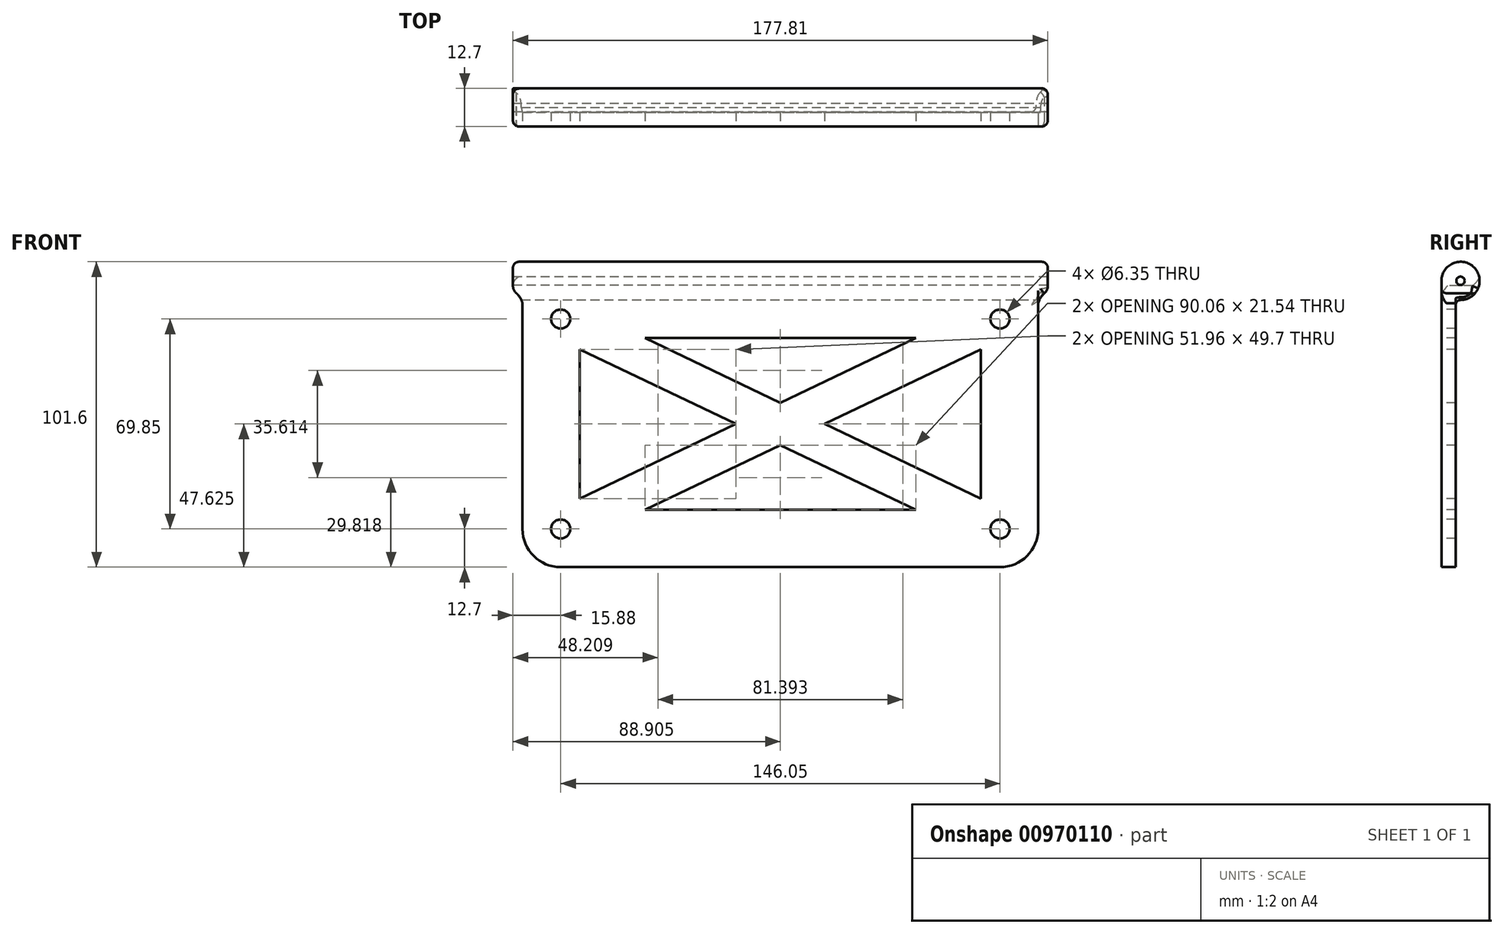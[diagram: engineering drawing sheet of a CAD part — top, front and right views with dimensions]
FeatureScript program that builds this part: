
annotation { "Feature Type Name" : "Feature", "Feature Type Description" : "" }
export const myFeature = defineFeature(function(context is Context, id is Id, definition is map)
    precondition{}
    {
        {
            var Q0;
            Q0=qCreatedBy(makeId("Front.planeOp"),FACE);
            var sketch = newSketch(context, id + "F0", { "sketchPlane" : qUnion([Q0])});
            skLineSegment(sketch, "E0", {"start": v(171.45, 127) * mm, "end": v(12.7, 127) * mm});
            skPoint(sketch, "E1.visualSharp", {"position": v(0, 127) * mm});
            skPoint(sketch, "E2.visualSharp", {"position": v(184.15, 127) * mm});
            skPoint(sketch, "E3.visualSharp", {"position": v(0, 0) * mm});
            skCircle(sketch, "E4", {"center": v(19.05, 107.95) * mm, "radius": 3.17 * mm});
            skCircle(sketch, "E5", {"center": v(165.1, 107.95) * mm, "radius": 3.18 * mm});
            skLineSegment(sketch, "E6", {"start": v(12.7, 127) * mm, "end": v(0, 127) * mm});
            skLineSegment(sketch, "E7", {"start": v(171.45, 127) * mm, "end": v(184.15, 127) * mm});
            skCircle(sketch, "E8", {"center": v(19.05, 38.1) * mm, "radius": 3.18 * mm});
            skCircle(sketch, "E9", {"center": v(165.1, 38.1) * mm, "radius": 3.18 * mm});
            skLineSegment(sketch, "E10", {"start": v(0, 127) * mm, "end": v(0, 25.4) * mm});
            skLineSegment(sketch, "E11", {"start": v(184.15, 127) * mm, "end": v(184.15, 25.4) * mm});
            skLineSegment(sketch, "E12", {"start": v(0, 25.4) * mm, "end": v(184.15, 25.4) * mm});
            skSolve(sketch);
        }
        {
            var Q0;
            Q0=makeQuery(id+"F0.imprint","IMPRINT",FACE,{"disambiguationData":[TD([[makeQuery(id+"F0.imprint","IMPRINT",EDGE,{"derivedFrom":sQuery(id+"F0.wireOp",EDGE,"Pz5NrIL3-ze5f-zlSV-9IkB-DhctpmxIF3Tt")}),1.0]])]});
            var Q1;
            Q1=makeQuery(id+"F0.imprint","IMPRINT",FACE,{"disambiguationData":[TD([[makeQuery(id+"F0.imprint","IMPRINT",EDGE,{"derivedFrom":sQuery(id+"F0.wireOp",EDGE,"E0")}),1.0]])]});
            extrude(context, id + "F1", {"entities" : qUnion([Q0, Q1]), "oppositeDirection" : true, "depth" : 12.7 * mm, "offsetDistance" : 25.4 * mm});
        }
        {
            var Q0;
            Q0=makeQuery(id+"F1.opExtrude","SWEPT_FACE",FACE,{"disambiguationData":[OSD([sQuery(id+"F0.wireOp",EDGE,"E11")])]});
            var sketch = newSketch(context, id + "F2", { "sketchPlane" : qUnion([Q0])});
            skLineSegment(sketch, "E13", {"start": v(6.35, 127) * mm, "end": v(6.35, 120.65) * mm});
            skArc(sketch, "E14", {"start": v(6.36, 114.3) * mm, "mid": v(7.15, 126.95) * mm, "end": v(4.76, 114.5) * mm});
            skLineSegment(sketch, "E15", {"start": v(0, 25.4) * mm, "end": v(4.76, 25.4) * mm});
            skLineSegment(sketch, "E16", {"start": v(4.76, 25.4) * mm, "end": v(4.76, 112.65) * mm});
            skArc(sketch, "E17", {"start": v(6.44, 114.3) * mm, "mid": v(5.26, 113.83) * mm, "end": v(4.76, 112.65) * mm});
            skCircle(sketch, "E18", {"center": v(6.35, 120.65) * mm, "radius": 1.4 * mm});
            skSolve(sketch);
        }
        {
            var Q0;
            Q0=makeQuery(id+"F1.opExtrude","CAP_FACE",FACE,{"disambiguationData":[OSD([sQuery(id+"F0.wireOp",EDGE,"E0"),sQuery(id+"F0.wireOp",EDGE,"E4"),sQuery(id+"F0.wireOp",EDGE,"E5"),sQuery(id+"F0.wireOp",EDGE,"E6"),sQuery(id+"F0.wireOp",EDGE,"E7"),sQuery(id+"F0.wireOp",EDGE,"E8"),sQuery(id+"F0.wireOp",EDGE,"E9"),sQuery(id+"F0.wireOp",EDGE,"E10"),sQuery(id+"F0.wireOp",EDGE,"E11"),sQuery(id+"F0.wireOp",EDGE,"E12")])],"isStart":true});
            var sketch = newSketch(context, id + "F3", { "sketchPlane" : qUnion([Q0])});
            skLineSegment(sketch, "E19", {"start": v(184.15, 127) * mm, "end": v(180.97, 127) * mm});
            skLineSegment(sketch, "E20", {"start": v(0, 127) * mm, "end": v(3.17, 127) * mm});
            skLineSegment(sketch, "E21", {"start": v(3.17, 127) * mm, "end": v(3.17, 118.95) * mm});
            skLineSegment(sketch, "E22", {"start": v(6.35, 25.4) * mm, "end": v(6.35, 113.16) * mm});
            skArc(sketch, "E23", {"start": v(3.17, 119.08) * mm, "mid": v(4.08, 116.8) * mm, "end": v(6.35, 115.84) * mm});
            skArc(sketch, "E24", {"start": v(6.35, 113.16) * mm, "mid": v(5.58, 115.04) * mm, "end": v(4.26, 116.57) * mm});
            skLineSegment(sketch, "E25", {"start": v(180.97, 127) * mm, "end": v(180.97, 118.95) * mm});
            skLineSegment(sketch, "E26", {"start": v(165.1, 38.1) * mm, "end": v(177.8, 38.1) * mm});
            skLineSegment(sketch, "E27", {"start": v(177.8, 25.4) * mm, "end": v(177.8, 127) * mm});
            skLineSegment(sketch, "E28", {"start": v(180.97, 118.95) * mm, "end": v(177.8, 118.95) * mm});
            skCircle(sketch, "E29", {"center": v(177.8, 118.95) * mm, "radius": 3.17 * mm});
            skArc(sketch, "E30", {"start": v(179.9, 116.57) * mm, "mid": v(178.58, 115.04) * mm, "end": v(177.8, 113.16) * mm});
            skLineSegment(sketch, "E31.trimOffspring", {"start": v(6.35, 115.84) * mm, "end": v(6.35, 127) * mm});
            skLineSegment(sketch, "E32", {"start": v(4.26, 116.57) * mm, "end": v(4.18, 116.7) * mm});
            skCircle(sketch, "E33", {"center": v(19.05, 38.1) * mm, "radius": 12.7 * mm});
            skCircle(sketch, "E34", {"center": v(165.1, 38.1) * mm, "radius": 12.7 * mm});
            skSolve(sketch);
        }
        {
            var Q0;
            {var subQ7=sQuery(id+"F3.wireOp",EDGE,"E20");Q0=makeQuery(id+"F3.imprint","IMPRINT",FACE,{"disambiguationData":[TD([[makeQuery(id+"F3.imprint","IMPRINT",EDGE,{"derivedFrom":subQ7}),-1.0]])]});}
            var Q1;
            Q1=makeQuery(id+"F3.imprint","IMPRINT",FACE,{"disambiguationData":[TD([[makeQuery(id+"F3.imprint","IMPRINT",EDGE,{"derivedFrom":sQuery(id+"F3.wireOp",EDGE,"E19")}),-1.0]])]});
            var Q2;
            {var subQ0=sQuery(id+"F3.wireOp",EDGE,"E22");var subQ1=makeQuery(id+"F1.opExtrude","CAP_EDGE",EDGE,{"disambiguationData":[OSD([sQuery(id+"F0.wireOp",EDGE,"E12")])],"isStart":true});var subQ2=makeQuery(id+"F3.imprint","INTERSECT",VERTEX,{"derivedFrom":[subQ1,subQ0]});Q2=makeQuery(id+"F3.imprint","IMPRINT",FACE,{"disambiguationData":[TD([[makeQuery(id+"F3.imprint","IMPRINT",EDGE,{"disambiguationData":[TD([[subQ2,-1.0]])],"derivedFrom":subQ0}),-1.0]])]});}
            var Q3;
            {var subQ0=sQuery(id+"F3.wireOp",EDGE,"E34");var subQ1=sQuery(id+"F3.wireOp",EDGE,"E27");var subQ2=makeQuery(id+"F3.imprint","INTERSECT",VERTEX,{"derivedFrom":[subQ1,subQ0]});Q3=makeQuery(id+"F3.imprint","IMPRINT",FACE,{"disambiguationData":[TD([[makeQuery(id+"F3.imprint","IMPRINT",EDGE,{"disambiguationData":[TD([[subQ2,1.0]])],"derivedFrom":subQ1}),1.0]])]});}
            extrude(context, id + "F4", {"entities" : qUnion([Q0, Q1, Q2, Q3]), "operationType" : NewBodyOperationType.REMOVE, "endBound" : BoundingType.THROUGH_ALL, "oppositeDirection" : true, "depth" : 25.4 * mm, "offsetDistance" : 25.4 * mm});
        }
        {
            var Q0;
            {var subQ3=sQuery(id+"F2.wireOp",EDGE,"E16");Q0=makeQuery(id+"F2.imprint","IMPRINT",FACE,{"disambiguationData":[TD([[makeQuery(id+"F2.imprint","IMPRINT",EDGE,{"derivedFrom":subQ3}),-1.0]])]});}
            var Q1;
            {var subQ0=sQuery(id+"F2.wireOp",EDGE,"E14");var subQ1=sQuery(id+"F0.wireOp",EDGE,"E11");var subQ4=makeQuery(id+"F1.opExtrude","CAP_EDGE",EDGE,{"disambiguationData":[OSD([subQ1])],"isStart":false});var subQ5=makeQuery(id+"F2.imprint","INTERSECT",VERTEX,{"derivedFrom":[subQ4,subQ0]});Q1=makeQuery(id+"F2.imprint","IMPRINT",FACE,{"disambiguationData":[TD([[makeQuery(id+"F2.imprint","IMPRINT",EDGE,{"disambiguationData":[TD([[subQ5,-1.0]])],"derivedFrom":subQ0}),-1.0]])]});}
            var Q2;
            {var subQ0=sQuery(id+"F2.wireOp",EDGE,"E14");var subQ1=sQuery(id+"F0.wireOp",EDGE,"E11");var subQ4=makeQuery(id+"F1.opExtrude","CAP_EDGE",EDGE,{"disambiguationData":[OSD([subQ1])],"isStart":true});var subQ5=makeQuery(id+"F2.imprint","INTERSECT",VERTEX,{"derivedFrom":[subQ4,subQ0]});Q2=makeQuery(id+"F2.imprint","IMPRINT",FACE,{"disambiguationData":[TD([[makeQuery(id+"F2.imprint","IMPRINT",EDGE,{"disambiguationData":[TD([[subQ5,1.0]])],"derivedFrom":subQ0}),-1.0]])]});}
            var Q3;
            Q3=makeQuery(id+"F2.imprint","IMPRINT",FACE,{"disambiguationData":[TD([[makeQuery(id+"F2.imprint","IMPRINT",EDGE,{"derivedFrom":sQuery(id+"F2.wireOp",EDGE,"E18")}),1.0]])]});
            extrude(context, id + "F5", {"entities" : qUnion([Q0, Q1, Q2, Q3]), "operationType" : NewBodyOperationType.REMOVE, "endBound" : BoundingType.THROUGH_ALL, "oppositeDirection" : true, "depth" : 25.4 * mm, "offsetDistance" : 25.4 * mm});
        }
        {
            var Q0;
            {var subQ0=sQuery(id+"F2.wireOp",EDGE,"E14");var subQ1=sQuery(id+"F0.wireOp",EDGE,"E11");var subQ3=makeQuery(id+"F2.imprint","INTERSECT",VERTEX,{"derivedFrom":[makeQuery(id+"F1.opExtrude","CAP_EDGE",EDGE,{"disambiguationData":[OSD([subQ1])],"isStart":false}),subQ0]});var subQ4=sQuery(id+"F2.wireOp",EDGE,"E17");var subQ5=makeQuery(id+"F2.imprint","INTERSECT",VERTEX,{"disambiguationData":[OD(1.0)],"derivedFrom":[subQ0,subQ4]});Q0=makeQuery(id+"F5.boolean.opBoolean","INTERSECT",EDGE,{"derivedFrom":[makeQuery(id+"F4.boolean.opBoolean","COPY",FACE,{"derivedFrom":makeQuery(id+"F4.opExtrude","SWEPT_FACE",FACE,{"disambiguationData":[OSD([sQuery(id+"F3.wireOp",EDGE,"E21")])]})}),makeQuery(id+"F5.opExtrude","SWEPT_FACE",FACE,{"disambiguationData":[OSD([subQ0]),TDD([makeQuery(id+"F2.imprint","IMPRINT",EDGE,{"disambiguationData":[TD([[makeQuery(id+"F2.imprint","INTERSECT",VERTEX,{"disambiguationData":[OD(0.0)],"derivedFrom":[subQ0,subQ4]}),-1.0]])],"derivedFrom":subQ0}),makeQuery(id+"F2.imprint","IMPRINT",EDGE,{"disambiguationData":[TD([[subQ5,-1.0]])],"derivedFrom":subQ0})])]}),makeQuery(id+"F5.opExtrude","SWEPT_FACE",FACE,{"disambiguationData":[OSD([subQ0]),TDD([makeQuery(id+"F2.imprint","IMPRINT",EDGE,{"disambiguationData":[TD([[subQ3,-1.0]])],"derivedFrom":subQ0})])]}),makeQuery(id+"F5.opExtrude","SWEPT_FACE",FACE,{"disambiguationData":[OSD([subQ0]),TDD([makeQuery(id+"F2.imprint","IMPRINT",EDGE,{"disambiguationData":[TD([[makeQuery(id+"F2.imprint","INTERSECT",VERTEX,{"derivedFrom":[makeQuery(id+"F1.opExtrude","CAP_EDGE",EDGE,{"disambiguationData":[OSD([subQ1])],"isStart":true}),subQ0]}),1.0]])],"derivedFrom":subQ0})])]})]});}
            var Q1;
            {var subQ0=sQuery(id+"F2.wireOp",EDGE,"E14");var subQ1=sQuery(id+"F0.wireOp",EDGE,"E11");var subQ3=makeQuery(id+"F2.imprint","INTERSECT",VERTEX,{"derivedFrom":[makeQuery(id+"F1.opExtrude","CAP_EDGE",EDGE,{"disambiguationData":[OSD([subQ1])],"isStart":false}),subQ0]});var subQ4=sQuery(id+"F2.wireOp",EDGE,"E17");var subQ5=makeQuery(id+"F2.imprint","INTERSECT",VERTEX,{"disambiguationData":[OD(1.0)],"derivedFrom":[subQ0,subQ4]});Q1=makeQuery(id+"F5.boolean.opBoolean","INTERSECT",EDGE,{"derivedFrom":[makeQuery(id+"F4.boolean.opBoolean","COPY",FACE,{"derivedFrom":makeQuery(id+"F4.opExtrude","SWEPT_FACE",FACE,{"disambiguationData":[OSD([sQuery(id+"F3.wireOp",EDGE,"E25")])]})}),makeQuery(id+"F5.opExtrude","SWEPT_FACE",FACE,{"disambiguationData":[OSD([subQ0]),TDD([makeQuery(id+"F2.imprint","IMPRINT",EDGE,{"disambiguationData":[TD([[makeQuery(id+"F2.imprint","INTERSECT",VERTEX,{"disambiguationData":[OD(0.0)],"derivedFrom":[subQ0,subQ4]}),-1.0]])],"derivedFrom":subQ0}),makeQuery(id+"F2.imprint","IMPRINT",EDGE,{"disambiguationData":[TD([[subQ5,-1.0]])],"derivedFrom":subQ0})])]}),makeQuery(id+"F5.opExtrude","SWEPT_FACE",FACE,{"disambiguationData":[OSD([subQ0]),TDD([makeQuery(id+"F2.imprint","IMPRINT",EDGE,{"disambiguationData":[TD([[subQ3,-1.0]])],"derivedFrom":subQ0})])]}),makeQuery(id+"F5.opExtrude","SWEPT_FACE",FACE,{"disambiguationData":[OSD([subQ0]),TDD([makeQuery(id+"F2.imprint","IMPRINT",EDGE,{"disambiguationData":[TD([[makeQuery(id+"F2.imprint","INTERSECT",VERTEX,{"derivedFrom":[makeQuery(id+"F1.opExtrude","CAP_EDGE",EDGE,{"disambiguationData":[OSD([subQ1])],"isStart":true}),subQ0]}),1.0]])],"derivedFrom":subQ0})])]})]});}
            fillet(context, id + "F6", {"entities" : qUnion([Q0, Q1]), "radius" : 2.03 * mm, "tangentPropagation" : true, "allowEdgeOverflow" : false});
        }
        {
            var Q0;
            Q0=makeQuery(id+"F1.opExtrude","CAP_FACE",FACE,{"disambiguationData":[OSD([sQuery(id+"F0.wireOp",EDGE,"E0"),sQuery(id+"F0.wireOp",EDGE,"E4"),sQuery(id+"F0.wireOp",EDGE,"E5"),sQuery(id+"F0.wireOp",EDGE,"E6"),sQuery(id+"F0.wireOp",EDGE,"E7"),sQuery(id+"F0.wireOp",EDGE,"E8"),sQuery(id+"F0.wireOp",EDGE,"E9"),sQuery(id+"F0.wireOp",EDGE,"E10"),sQuery(id+"F0.wireOp",EDGE,"E11"),sQuery(id+"F0.wireOp",EDGE,"E12")])],"isStart":true});
            var sketch = newSketch(context, id + "F7", { "sketchPlane" : qUnion([Q0])});
            skLineSegment(sketch, "E35.bottom", {"start": v(19.05, 107.95) * mm, "end": v(165.1, 107.95) * mm});
            skLineSegment(sketch, "E35.top", {"start": v(19.05, 38.1) * mm, "end": v(165.1, 38.1) * mm});
            skLineSegment(sketch, "E35.left", {"start": v(19.05, 107.95) * mm, "end": v(19.05, 38.1) * mm});
            skLineSegment(sketch, "E35.right", {"start": v(165.1, 107.95) * mm, "end": v(165.1, 38.1) * mm});
            skLineSegment(sketch, "E36", {"start": v(19.05, 38.1) * mm, "end": v(165.1, 107.95) * mm});
            skLineSegment(sketch, "E37", {"start": v(19.05, 107.95) * mm, "end": v(165.1, 38.1) * mm});
            skLineSegment(sketch, "E38.0", {"start": v(16.31, 102.22) * mm, "end": v(162.36, 32.37) * mm});
            skLineSegment(sketch, "E39.0", {"start": v(21.79, 113.68) * mm, "end": v(167.84, 43.83) * mm});
            skLineSegment(sketch, "E40.0", {"start": v(21.79, 32.37) * mm, "end": v(167.84, 102.22) * mm});
            skLineSegment(sketch, "E41.0", {"start": v(16.31, 43.83) * mm, "end": v(162.36, 113.68) * mm});
            skLineSegment(sketch, "E42.0", {"start": v(25.4, 107.95) * mm, "end": v(25.4, 38.1) * mm});
            skLineSegment(sketch, "E43.0", {"start": v(19.05, 101.6) * mm, "end": v(165.1, 101.6) * mm});
            skLineSegment(sketch, "E44.0", {"start": v(158.75, 107.95) * mm, "end": v(158.75, 38.1) * mm});
            skLineSegment(sketch, "E45.0", {"start": v(19.05, 44.45) * mm, "end": v(165.1, 44.45) * mm});
            skSolve(sketch);
        }
        {
            var Q0;
            {var subQ0=sQuery(id+"F7.wireOp",EDGE,"E43.0");var subQ1=sQuery(id+"F7.wireOp",EDGE,"E39.0");var subQ2=makeQuery(id+"F7.imprint","INTERSECT",VERTEX,{"derivedFrom":[subQ1,subQ0]});Q0=makeQuery(id+"F7.imprint","IMPRINT",FACE,{"disambiguationData":[TD([[makeQuery(id+"F7.imprint","IMPRINT",EDGE,{"disambiguationData":[TD([[subQ2,-1.0]])],"derivedFrom":subQ1}),1.0]])]});}
            var Q1;
            {var subQ0=sQuery(id+"F7.wireOp",EDGE,"E42.0");var subQ1=sQuery(id+"F7.wireOp",EDGE,"E38.0");var subQ2=makeQuery(id+"F7.imprint","INTERSECT",VERTEX,{"derivedFrom":[subQ1,subQ0]});Q1=makeQuery(id+"F7.imprint","IMPRINT",FACE,{"disambiguationData":[TD([[makeQuery(id+"F7.imprint","IMPRINT",EDGE,{"disambiguationData":[TD([[subQ2,-1.0]])],"derivedFrom":subQ1}),-1.0]])]});}
            var Q2;
            {var subQ0=sQuery(id+"F7.wireOp",EDGE,"E40.0");var subQ1=sQuery(id+"F7.wireOp",EDGE,"E38.0");var subQ2=makeQuery(id+"F7.imprint","INTERSECT",VERTEX,{"derivedFrom":[subQ1,subQ0]});Q2=makeQuery(id+"F7.imprint","IMPRINT",FACE,{"disambiguationData":[TD([[makeQuery(id+"F7.imprint","IMPRINT",EDGE,{"disambiguationData":[TD([[subQ2,-1.0]])],"derivedFrom":subQ1}),-1.0]])]});}
            var Q3;
            {var subQ0=sQuery(id+"F7.wireOp",EDGE,"E40.0");var subQ1=sQuery(id+"F7.wireOp",EDGE,"E39.0");var subQ2=makeQuery(id+"F7.imprint","INTERSECT",VERTEX,{"derivedFrom":[subQ1,subQ0]});Q3=makeQuery(id+"F7.imprint","IMPRINT",FACE,{"disambiguationData":[TD([[makeQuery(id+"F7.imprint","IMPRINT",EDGE,{"disambiguationData":[TD([[subQ2,-1.0]])],"derivedFrom":subQ1}),1.0]])]});}
            extrude(context, id + "F8", {"entities" : qUnion([Q0, Q1, Q2, Q3]), "operationType" : NewBodyOperationType.REMOVE, "endBound" : BoundingType.THROUGH_ALL, "oppositeDirection" : true, "depth" : 25.4 * mm, "offsetDistance" : 25.4 * mm});
        }
    });
